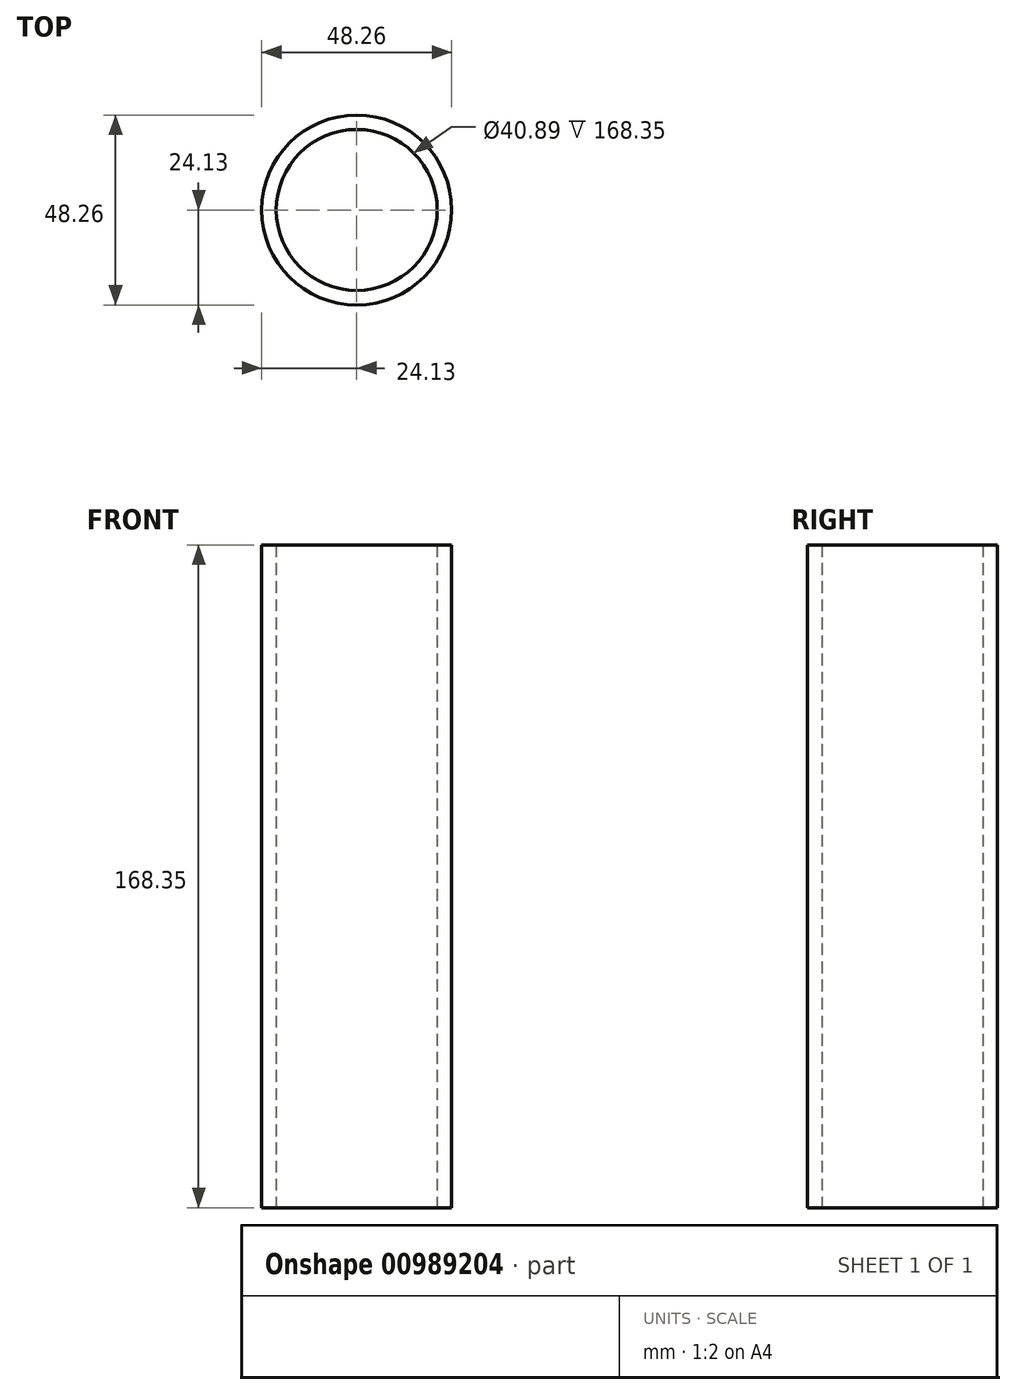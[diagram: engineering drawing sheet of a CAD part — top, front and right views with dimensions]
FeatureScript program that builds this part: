
annotation { "Feature Type Name" : "Feature", "Feature Type Description" : "" }
export const myFeature = defineFeature(function(context is Context, id is Id, definition is map)
    precondition{}
    {
        {
            var Q0;
            Q0=qCreatedBy(makeId("Top.planeOp"),FACE);
            var sketch = newSketch(context, id + "F0", { "sketchPlane" : qUnion([Q0])});
            skCircle(sketch, "E0", {"center": v(0, -400) * mm, "radius": 24.13 * mm});
            skCircle(sketch, "E1", {"center": v(0, -400) * mm, "radius": 20.45 * mm});
            skSolve(sketch);
        }
        {
            var Q0;
            Q0 = qSketchRegion(id + "F0", true);
            extrude(context, id + "F1", {"entities" : qUnion([Q0]), "depth" : 150 * mm + 18.35 * mm, "offsetDistance" : 25 * mm});
        }
    });
